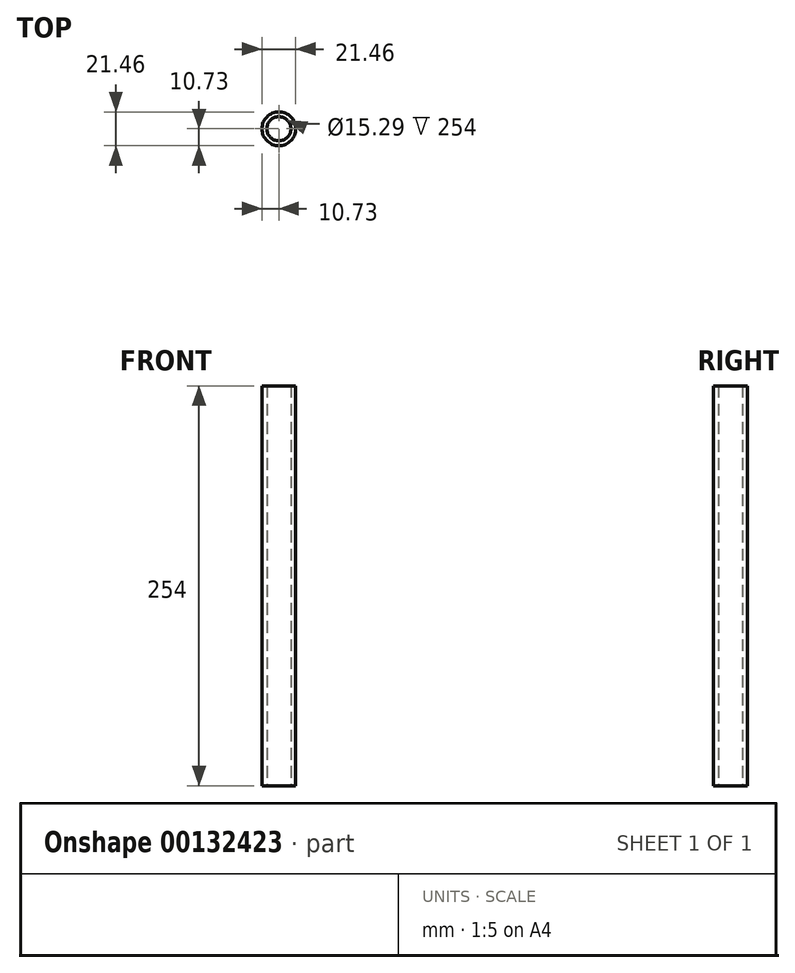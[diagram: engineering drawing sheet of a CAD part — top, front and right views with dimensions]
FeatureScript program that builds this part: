
annotation { "Feature Type Name" : "Feature", "Feature Type Description" : "" }
export const myFeature = defineFeature(function(context is Context, id is Id, definition is map)
    precondition{}
    {
        {
            var Q0;
            Q0=qCreatedBy(makeId("Top.planeOp"),FACE);
            var sketch = newSketch(context, id + "F0", { "sketchPlane" : qUnion([Q0])});
            skCircle(sketch, "E0", {"center": v(0, 0) * mm, "radius": 10.73 * mm});
            skCircle(sketch, "E1", {"center": v(0, 0) * mm, "radius": 7.65 * mm});
            skSolve(sketch);
        }
        {
            var Q0;
            Q0=makeQuery(id+"F0.imprint","IMPRINT",FACE,{"disambiguationData":[TD([[makeQuery(id+"F0.imprint","IMPRINT",EDGE,{"derivedFrom":sQuery(id+"F0.wireOp",EDGE,"E0")}),1.0]])]});
            extrude(context, id + "F1", {"entities" : qUnion([Q0]), "depth" : 254 * mm});
        }
    });
